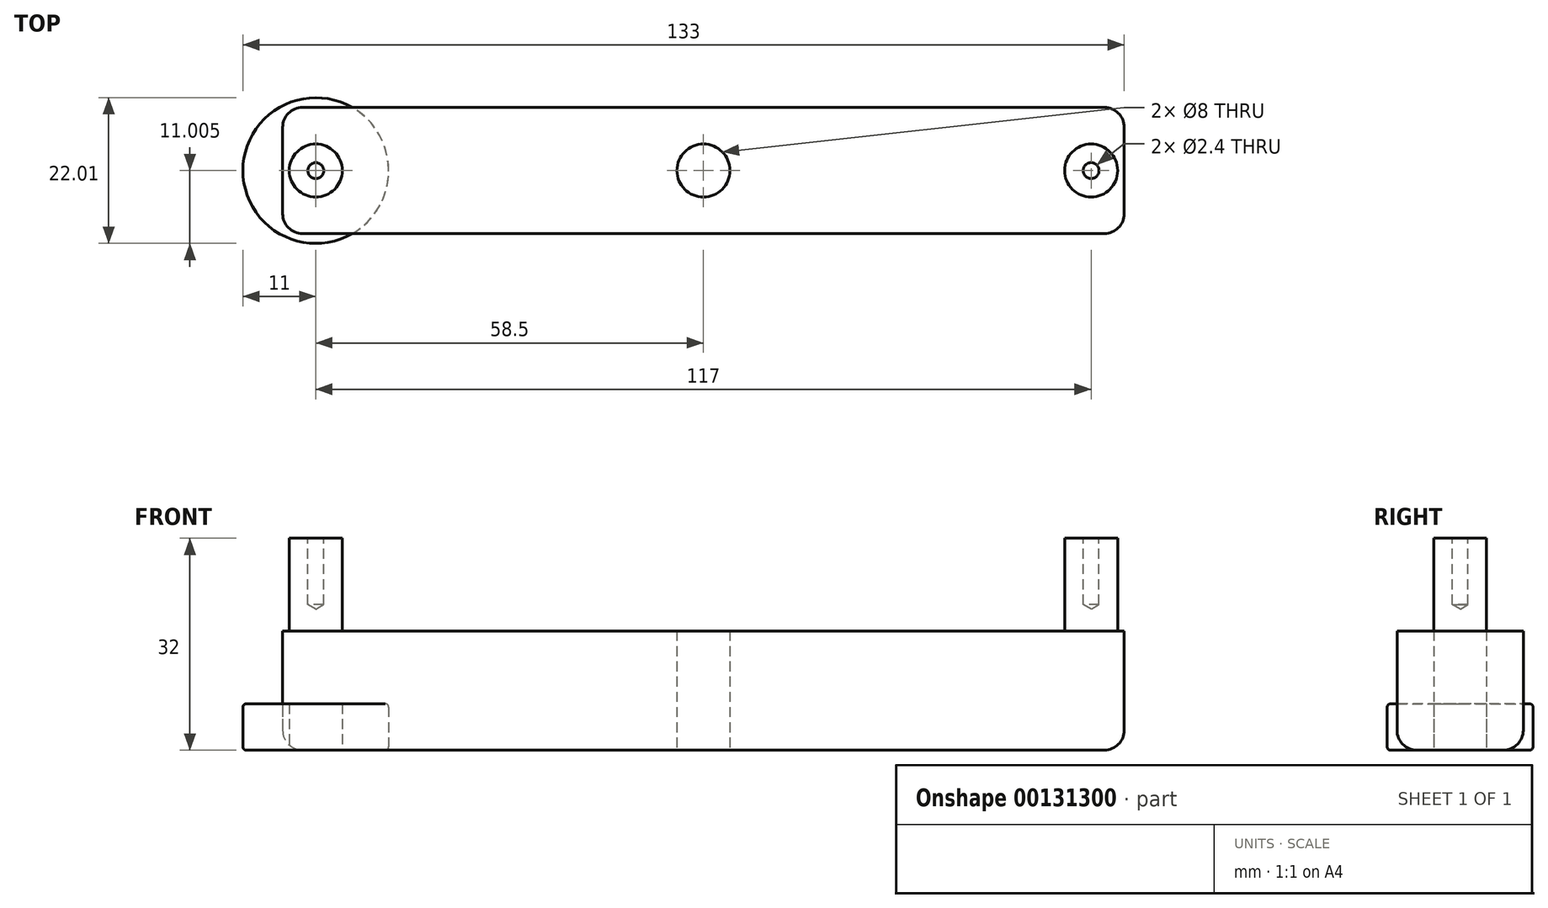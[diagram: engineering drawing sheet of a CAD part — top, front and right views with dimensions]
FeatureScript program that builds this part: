
annotation { "Feature Type Name" : "Feature", "Feature Type Description" : "" }
export const myFeature = defineFeature(function(context is Context, id is Id, definition is map)
    precondition{}
    {
        {
            var Q0;
            Q0=qCreatedBy(makeId("Top.planeOp"),FACE);
            var sketch = newSketch(context, id + "F0", { "sketchPlane" : qUnion([Q0])});
            skLineSegment(sketch, "E0.bottom", {"start": v(0, 0) * mm, "end": v(127, 0) * mm});
            skLineSegment(sketch, "E0.top", {"start": v(0, -19.05) * mm, "end": v(127, -19.05) * mm});
            skLineSegment(sketch, "E0.left", {"start": v(0, 0) * mm, "end": v(0, -19.05) * mm});
            skLineSegment(sketch, "E0.right", {"start": v(127, 0) * mm, "end": v(127, -19.05) * mm});
            skCircle(sketch, "E1", {"center": v(5, -9.53) * mm, "radius": 4 * mm});
            skCircle(sketch, "E2", {"center": v(122, -9.52) * mm, "radius": 4 * mm});
            skPoint(sketch, "E2.centerSnap0", {"position": v(127, -9.52) * mm});
            skCircle(sketch, "E3", {"center": v(5, -9.53) * mm, "radius": 11 * mm, "construction": true});
            skCircle(sketch, "E4", {"center": v(122, -9.52) * mm, "radius": 11 * mm, "construction": true});
            skCircle(sketch, "E5", {"center": v(63.5, -9.53) * mm, "radius": 4 * mm});
            skPoint(sketch, "E5.centerSnap0", {"position": v(63.5, -19.05) * mm});
            skSolve(sketch);
        }
        {
            var Q0;
            Q0=makeQuery(id+"F0.imprint","IMPRINT",FACE,{"disambiguationData":[TD([[makeQuery(id+"F0.imprint","IMPRINT",EDGE,{"derivedFrom":sQuery(id+"F0.wireOp",EDGE,"E1")}),1.0]])]});
            var Q1;
            Q1=makeQuery(id+"F0.imprint","IMPRINT",FACE,{"disambiguationData":[TD([[makeQuery(id+"F0.imprint","IMPRINT",EDGE,{"derivedFrom":sQuery(id+"F0.wireOp",EDGE,"E0.bottom")}),-1.0]])]});
            var Q2;
            Q2=makeQuery(id+"F0.imprint","IMPRINT",FACE,{"disambiguationData":[TD([[makeQuery(id+"F0.imprint","IMPRINT",EDGE,{"derivedFrom":sQuery(id+"F0.wireOp",EDGE,"E2")}),1.0]])]});
            extrude(context, id + "F1", {"entities" : qUnion([Q0, Q1, Q2]), "depth" : 18 * mm});
        }
        {
            var Q0;
            Q0=makeQuery(id+"F0.imprint","IMPRINT",FACE,{"disambiguationData":[TD([[makeQuery(id+"F0.imprint","IMPRINT",EDGE,{"derivedFrom":sQuery(id+"F0.wireOp",EDGE,"E1")}),1.0]])]});
            var Q1;
            Q1=makeQuery(id+"F0.imprint","IMPRINT",FACE,{"disambiguationData":[TD([[makeQuery(id+"F0.imprint","IMPRINT",EDGE,{"derivedFrom":sQuery(id+"F0.wireOp",EDGE,"E2")}),1.0]])]});
            extrude(context, id + "F2", {"entities" : qUnion([Q0, Q1]), "operationType" : NewBodyOperationType.ADD, "depth" : 18 * mm + 14 * mm});
        }
        {
            var Q0;
            Q0=makeQuery(id+"F2.opExtrude","CAP_FACE",FACE,{"disambiguationData":[OSD([sQuery(id+"F0.wireOp",EDGE,"E1")])],"isStart":false});
            var sketch = newSketch(context, id + "F3", { "sketchPlane" : qUnion([Q0])});
            skPoint(sketch, "E6.0", {"position": v(5, -9.53) * mm});
            skPoint(sketch, "E7.0", {"position": v(122, -9.52) * mm});
            skSolve(sketch);
        }
        {
            var Q0;
            Q0=sQuery(id+"F3.wireOp",VERTEX,"E6.0");
            var Q1;
            Q1=sQuery(id+"F3.wireOp",VERTEX,"E7.0");
            var Q2;
            Q2=makeQuery(id+"F1.opExtrude","SWEPT_BODY",BODY,{"disambiguationData":[OSD([sQuery(id+"F0.wireOp",EDGE,"E0.bottom"),sQuery(id+"F0.wireOp",EDGE,"E0.top"),sQuery(id+"F0.wireOp",EDGE,"E0.left"),sQuery(id+"F0.wireOp",EDGE,"E0.right")])]});
            hole(context, id + "F4", {"style" : HoleStyle.SIMPLE, "endStyle" : HoleEndStyle.BLIND, "standardTappedOrClearance" : lookupTablePath({ "standard" : "ISO", "engagement" : "75%", "pitch" : "0.6 mm", "size" : "M3", "type" : "Tapped" }), "standardBlindInLast" : lookupTablePath({ "standard" : "ISO", "engagement" : "75%", "pitch" : "0.6 mm", "size" : "M3", "type" : "Tapped" }), "holeDiameter" : 2.4 * mm, "holeDepth" : 10 * mm, "startFromSketch" : true, "locations" : qUnion([Q0, Q1]), "scope" : qUnion([Q2])});
        }
        {
            var Q0;
            Q0=makeQuery(id+"F1.opExtrude","SWEPT_EDGE",EDGE,{"disambiguationData":[OSD([sQuery(id+"F0.wireOp",EDGE,"E0.top"),sQuery(id+"F0.wireOp",EDGE,"E0.right")])]});
            var Q1;
            Q1=makeQuery(id+"F1.opExtrude","SWEPT_EDGE",EDGE,{"disambiguationData":[OSD([sQuery(id+"F0.wireOp",EDGE,"E0.bottom"),sQuery(id+"F0.wireOp",EDGE,"E0.right")])]});
            var Q2;
            Q2=makeQuery(id+"F1.opExtrude","SWEPT_EDGE",EDGE,{"disambiguationData":[OSD([sQuery(id+"F0.wireOp",EDGE,"E0.bottom"),sQuery(id+"F0.wireOp",EDGE,"E0.left")])]});
            var Q3;
            Q3=makeQuery(id+"F1.opExtrude","SWEPT_EDGE",EDGE,{"disambiguationData":[OSD([sQuery(id+"F0.wireOp",EDGE,"E0.top"),sQuery(id+"F0.wireOp",EDGE,"E0.left")])]});
            var Q4;
            Q4=makeQuery(id+"F1.opExtrude","CAP_EDGE",EDGE,{"disambiguationData":[OSD([sQuery(id+"F0.wireOp",EDGE,"E0.top")])],"isStart":true});
            var Q5;
            Q5=makeQuery(id+"F1.opExtrude","CAP_EDGE",EDGE,{"disambiguationData":[OSD([sQuery(id+"F0.wireOp",EDGE,"E0.bottom")])],"isStart":true});
            var Q6;
            Q6=makeQuery(id+"F1.opExtrude","CAP_EDGE",EDGE,{"disambiguationData":[OSD([sQuery(id+"F0.wireOp",EDGE,"E0.left")])],"isStart":true});
            var Q7;
            Q7=makeQuery(id+"F1.opExtrude","CAP_EDGE",EDGE,{"disambiguationData":[OSD([sQuery(id+"F0.wireOp",EDGE,"E0.right")])],"isStart":true});
            fillet(context, id + "F5", {"entities" : qUnion([Q0, Q1, Q2, Q3, Q4, Q5, Q6, Q7]), "radius" : 3 * mm, "tangentPropagation" : true, "allowEdgeOverflow" : false});
        }
        {
            var Q0;
            Q0=qCreatedBy(makeId("Top.planeOp"),FACE);
            var sketch = newSketch(context, id + "F6", { "sketchPlane" : qUnion([Q0])});
            skCircle(sketch, "E8.0", {"center": v(5, -9.53) * mm, "radius": 11 * mm});
            skCircle(sketch, "E9.0", {"center": v(5, -9.53) * mm, "radius": 4 * mm});
            skSolve(sketch);
        }
        {
            var Q0;
            Q0 = qSketchRegion(id + "F6", true);
            extrude(context, id + "F7", {"entities" : qUnion([Q0]), "depth" : 7 * mm});
        }
        {
            var Q0;
            Q0=makeQuery(id+"F7.opExtrude","CAP_EDGE",EDGE,{"disambiguationData":[OSD([sQuery(id+"F6.wireOp",EDGE,"E8.0")])],"isStart":false});
            var Q1;
            Q1=makeQuery(id+"F7.opExtrude","CAP_EDGE",EDGE,{"disambiguationData":[OSD([sQuery(id+"F6.wireOp",EDGE,"E8.0")])],"isStart":true});
            fillet(context, id + "F8", {"entities" : qUnion([Q0, Q1]), "radius" : 0.5 * mm, "tangentPropagation" : true, "allowEdgeOverflow" : false});
        }
    });
